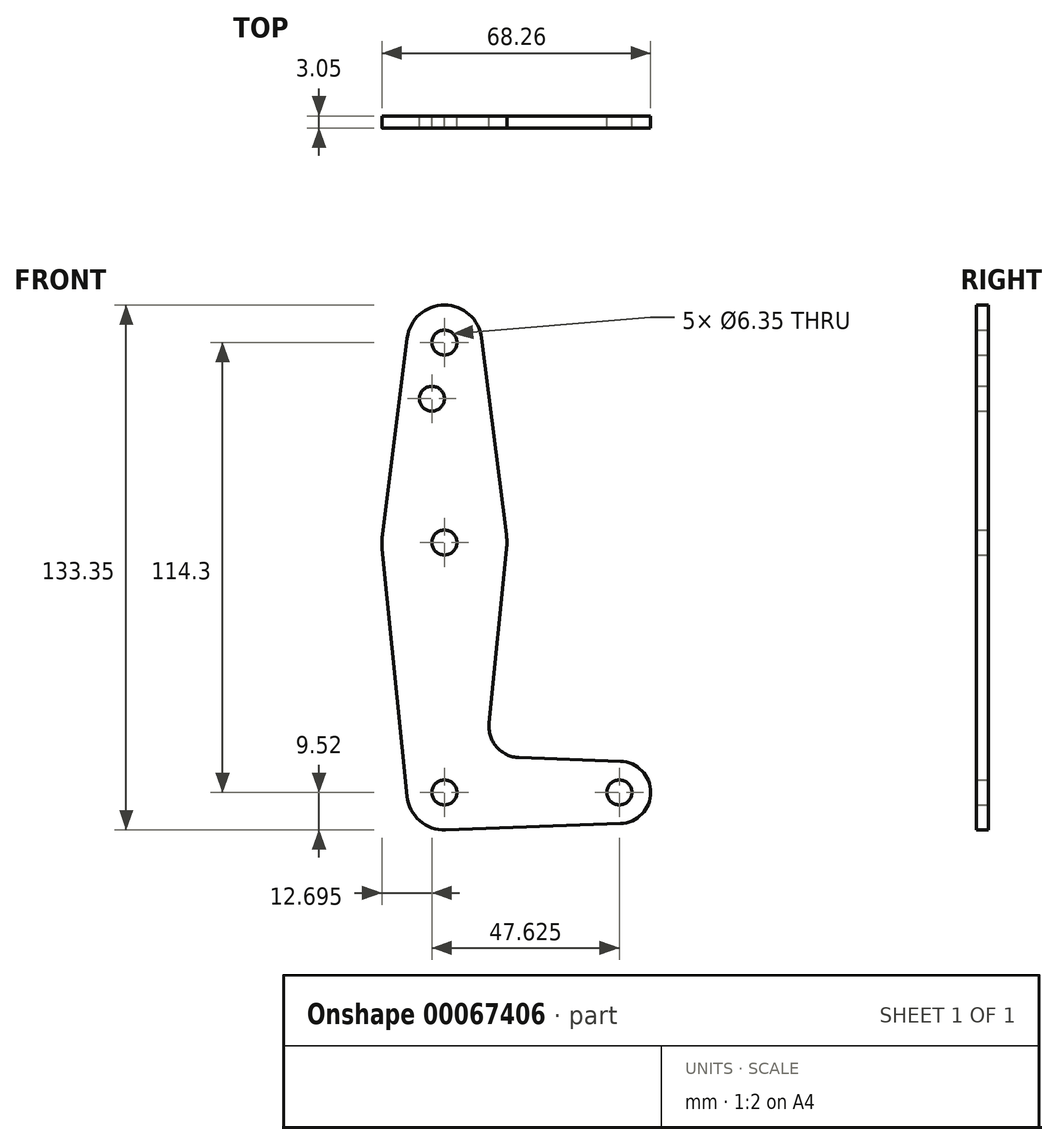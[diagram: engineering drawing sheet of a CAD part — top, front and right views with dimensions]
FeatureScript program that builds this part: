
annotation { "Feature Type Name" : "Feature", "Feature Type Description" : "" }
export const myFeature = defineFeature(function(context is Context, id is Id, definition is map)
    precondition{}
    {
        {
            var Q0;
            Q0=qCreatedBy(makeId("Front.planeOp"),FACE);
            var sketch = newSketch(context, id + "F0", { "sketchPlane" : qUnion([Q0])});
            skLineSegment(sketch, "E0", {"start": v(0, 0) * mm, "end": v(44.45, 0) * mm, "construction": true});
            skLineSegment(sketch, "E1", {"start": v(0, 0) * mm, "end": v(0, 114.3) * mm, "construction": true});
            skCircle(sketch, "E2", {"center": v(0, 114.3) * mm, "radius": 9.53 * mm});
            skCircle(sketch, "E3", {"center": v(0, 63.5) * mm, "radius": 15.88 * mm});
            skCircle(sketch, "E4", {"center": v(0, 0) * mm, "radius": 9.53 * mm});
            skCircle(sketch, "E5", {"center": v(44.45, 0) * mm, "radius": 7.94 * mm});
            skLineSegment(sketch, "E6", {"start": v(9.45, 115.5) * mm, "end": v(15.75, 65.48) * mm});
            skLineSegment(sketch, "E7", {"start": v(15.8, 61.91) * mm, "end": v(11.34, 17.6) * mm});
            skLineSegment(sketch, "E8", {"start": v(-9.45, 115.5) * mm, "end": v(-15.75, 65.48) * mm});
            skLineSegment(sketch, "E9", {"start": v(-15.8, 61.91) * mm, "end": v(-9.48, -0.95) * mm});
            skLineSegment(sketch, "E10", {"start": v(18.97, 8.85) * mm, "end": v(44.73, 7.93) * mm});
            skLineSegment(sketch, "E11", {"start": v(44.73, -7.93) * mm, "end": v(0.34, -9.52) * mm});
            skCircle(sketch, "E12", {"center": v(0, 114.3) * mm, "radius": 3.18 * mm});
            skCircle(sketch, "E13", {"center": v(0, 63.5) * mm, "radius": 3.18 * mm});
            skCircle(sketch, "E14", {"center": v(-3.18, 100.03) * mm, "radius": 3.18 * mm});
            skCircle(sketch, "E15", {"center": v(0, 0) * mm, "radius": 3.18 * mm});
            skCircle(sketch, "E16", {"center": v(44.45, 0) * mm, "radius": 3.18 * mm});
            skArc(sketch, "E17.filletArc", {"start": v(11.34, 17.6) * mm, "mid": v(13.26, 11.57) * mm, "end": v(18.97, 8.85) * mm});
            skSolve(sketch);
        }
        {
            var Q0;
            Q0 = qSketchRegion(id + "F0", true);
            extrude(context, id + "F1", {"entities" : qUnion([Q0]), "depth" : 3.05 * mm});
        }
    });
